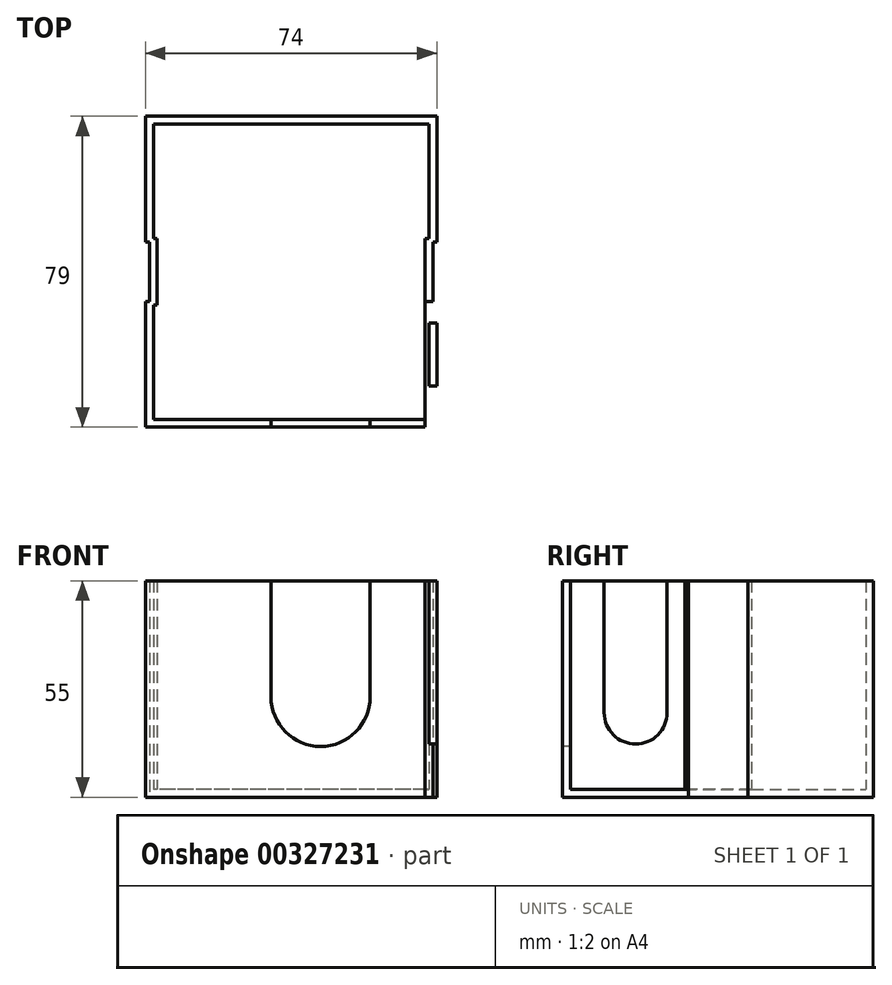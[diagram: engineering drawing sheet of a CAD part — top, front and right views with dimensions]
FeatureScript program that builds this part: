
annotation { "Feature Type Name" : "Feature", "Feature Type Description" : "" }
export const myFeature = defineFeature(function(context is Context, id is Id, definition is map)
    precondition{}
    {
        {
            var Q0;
            Q0=qCreatedBy(makeId("Top.planeOp"),FACE);
            var sketch = newSketch(context, id + "F0", { "sketchPlane" : qUnion([Q0])});
            skLineSegment(sketch, "E0.bottom", {"start": v(35, -37.5) * mm, "end": v(-35, -37.5) * mm});
            skLineSegment(sketch, "E0.top", {"start": v(35, 37.5) * mm, "end": v(-35, 37.5) * mm});
            skLineSegment(sketch, "E0.left", {"start": v(35, -37.5) * mm, "end": v(35, -8.5) * mm});
            skLineSegment(sketch, "E0.right", {"start": v(-35, -37.5) * mm, "end": v(-35, -8.5) * mm});
            skPoint(sketch, "E0.middle", {"position": v(0, 0) * mm});
            skLineSegment(sketch, "E1.bottom", {"start": v(37, -39.5) * mm, "end": v(-37, -39.5) * mm});
            skLineSegment(sketch, "E1.top", {"start": v(37, 39.5) * mm, "end": v(-37, 39.5) * mm});
            skLineSegment(sketch, "E1.left", {"start": v(37, -39.5) * mm, "end": v(37, -7.5) * mm});
            skLineSegment(sketch, "E1.right", {"start": v(-37, -39.5) * mm, "end": v(-37, -7.5) * mm});
            skLineSegment(sketch, "E2.top", {"start": v(37, 7.5) * mm, "end": v(36, 7.5) * mm});
            skLineSegment(sketch, "E2.right", {"start": v(36, 0) * mm, "end": v(36, 7.5) * mm});
            skPoint(sketch, "E2.left.start.orphan", {"position": v(37, 0) * mm});
            skLineSegment(sketch, "E3.trimOffspring", {"start": v(37, 7.5) * mm, "end": v(37, 39.5) * mm});
            skLineSegment(sketch, "E4.MirrorCS", {"start": v(36, 0) * mm, "end": v(36, -7.5) * mm});
            skLineSegment(sketch, "E5.MirrorCS", {"start": v(37, -7.5) * mm, "end": v(36, -7.5) * mm});
            skLineSegment(sketch, "E6.MirrorCS", {"start": v(-37, 7.5) * mm, "end": v(-36, 7.5) * mm});
            skLineSegment(sketch, "E7.MirrorCS", {"start": v(-36, 0) * mm, "end": v(-36, 7.5) * mm});
            skLineSegment(sketch, "E8.MirrorCS", {"start": v(-37, -7.5) * mm, "end": v(-36, -7.5) * mm});
            skLineSegment(sketch, "E9.MirrorCS", {"start": v(-36, 0) * mm, "end": v(-36, -7.5) * mm});
            skLineSegment(sketch, "E10.trimOffspring", {"start": v(-37, 7.5) * mm, "end": v(-37, 39.5) * mm});
            skLineSegment(sketch, "E11.bottom", {"start": v(34, 0) * mm, "end": v(35, 0) * mm});
            skLineSegment(sketch, "E11.top", {"start": v(34, -8.5) * mm, "end": v(35, -8.5) * mm});
            skLineSegment(sketch, "E11.left", {"start": v(34, 0) * mm, "end": v(34, -8.5) * mm});
            skLineSegment(sketch, "E12.MirrorCS", {"start": v(34, 0) * mm, "end": v(34, 8.5) * mm});
            skLineSegment(sketch, "E13.MirrorCS", {"start": v(34, 8.5) * mm, "end": v(35, 8.5) * mm});
            skLineSegment(sketch, "E14.trimOffspring", {"start": v(35, 8.5) * mm, "end": v(35, 37.5) * mm});
            skLineSegment(sketch, "E15.MirrorCS", {"start": v(-34, 8.5) * mm, "end": v(-35, 8.5) * mm});
            skLineSegment(sketch, "E16.MirrorCS", {"start": v(-34, -8.5) * mm, "end": v(-35, -8.5) * mm});
            skLineSegment(sketch, "E17.MirrorCS", {"start": v(-34, 0) * mm, "end": v(-34, 8.5) * mm});
            skLineSegment(sketch, "E18.MirrorCS", {"start": v(-34, 0) * mm, "end": v(-34, -8.5) * mm});
            skLineSegment(sketch, "E19.trimOffspring", {"start": v(-35, 8.5) * mm, "end": v(-35, 37.5) * mm});
            skSolve(sketch);
        }
        {
            var Q0;
            Q0=makeQuery(id+"F0.imprint","IMPRINT",FACE,{"disambiguationData":[TD([[makeQuery(id+"F0.imprint","IMPRINT",EDGE,{"derivedFrom":sQuery(id+"F0.wireOp",EDGE,"E0.bottom")}),-1.0]])]});
            extrude(context, id + "F1", {"entities" : qUnion([Q0]), "depth" : 2 * mm});
        }
        {
            var Q0;
            Q0=makeQuery(id+"F0.imprint","IMPRINT",FACE,{"disambiguationData":[TD([[makeQuery(id+"F0.imprint","IMPRINT",EDGE,{"derivedFrom":sQuery(id+"F0.wireOp",EDGE,"E0.bottom")}),1.0]])]});
            extrude(context, id + "F2", {"entities" : qUnion([Q0]), "operationType" : NewBodyOperationType.ADD, "depth" : 55 * mm});
        }
        {
            var Q0;
            Q0=makeQuery(id+"F2.opExtrude","SWEPT_FACE",FACE,{"disambiguationData":[OSD([sQuery(id+"F0.wireOp",EDGE,"E1.bottom")])]});
            var sketch = newSketch(context, id + "F3", { "sketchPlane" : qUnion([Q0])});
            skLineSegment(sketch, "E20", {"start": v(-102.96, 2) * mm, "end": v(100.81, 2) * mm, "construction": true});
            skLineSegment(sketch, "E21", {"start": v(35, 67.48) * mm, "end": v(35, -8.87) * mm, "construction": true});
            skLineSegment(sketch, "E22", {"start": v(15, 18) * mm, "end": v(61.68, 18) * mm, "construction": true});
            skLineSegment(sketch, "E23.trimOffspring", {"start": v(15, 18) * mm, "end": v(15, -13.29) * mm, "construction": true});
            skArc(sketch, "E24.0", {"start": v(-5.12, 25.5) * mm, "mid": v(7.49, 12.9) * mm, "end": v(20.1, 25.5) * mm});
            skLineSegment(sketch, "E25", {"start": v(-5.12, 25.5) * mm, "end": v(-5.12, 55) * mm});
            skLineSegment(sketch, "E26", {"start": v(20.1, 25.5) * mm, "end": v(20.1, 55) * mm});
            skLineSegment(sketch, "E27", {"start": v(20.1, 55) * mm, "end": v(-5.12, 55) * mm});
            skSolve(sketch);
        }
        {
            var Q0;
            Q0=makeQuery(id+"F3.imprint","IMPRINT",FACE,{"disambiguationData":[TD([[makeQuery(id+"F3.imprint","IMPRINT",EDGE,{"derivedFrom":sQuery(id+"F3.wireOp",EDGE,"E24.0")}),1.0]])]});
            extrude(context, id + "F4", {"entities" : qUnion([Q0]), "operationType" : NewBodyOperationType.REMOVE, "oppositeDirection" : true, "depth" : 3 * mm});
        }
        {
            var Q0;
            Q0=makeQuery(id+"F2.opExtrude","SWEPT_FACE",FACE,{"disambiguationData":[OSD([sQuery(id+"F0.wireOp",EDGE,"E1.left")])]});
            var sketch = newSketch(context, id + "F5", { "sketchPlane" : qUnion([Q0])});
            skLineSegment(sketch, "E28", {"start": v(-240.47, 2) * mm, "end": v(230.5, 2) * mm, "construction": true});
            skLineSegment(sketch, "E29", {"start": v(-37.5, 167.9) * mm, "end": v(-37.5, -121.1) * mm, "construction": true});
            skPoint(sketch, "E30", {"position": v(-20.98, 21.5) * mm});
            skLineSegment(sketch, "E31", {"start": v(-44.58, 21.5) * mm, "end": v(2.63, 21.5) * mm, "construction": true});
            skArc(sketch, "E32", {"start": v(-12.98, 21.5) * mm, "mid": v(-20.98, 13.5) * mm, "end": v(-28.98, 21.5) * mm});
            skLineSegment(sketch, "E33", {"start": v(-28.98, 21.5) * mm, "end": v(-28.98, 55) * mm});
            skLineSegment(sketch, "E34", {"start": v(-12.98, 21.5) * mm, "end": v(-12.98, 55) * mm});
            skLineSegment(sketch, "E35", {"start": v(-28.98, 55) * mm, "end": v(-12.98, 55) * mm});
            skSolve(sketch);
        }
        {
            var Q0;
            Q0=makeQuery(id+"F5.imprint","IMPRINT",FACE,{"disambiguationData":[TD([[makeQuery(id+"F5.imprint","IMPRINT",EDGE,{"derivedFrom":sQuery(id+"F5.wireOp",EDGE,"E32")}),-1.0]])]});
            extrude(context, id + "F6", {"entities" : qUnion([Q0]), "operationType" : NewBodyOperationType.REMOVE, "oppositeDirection" : true, "depth" : 3 * mm});
        }
    });
